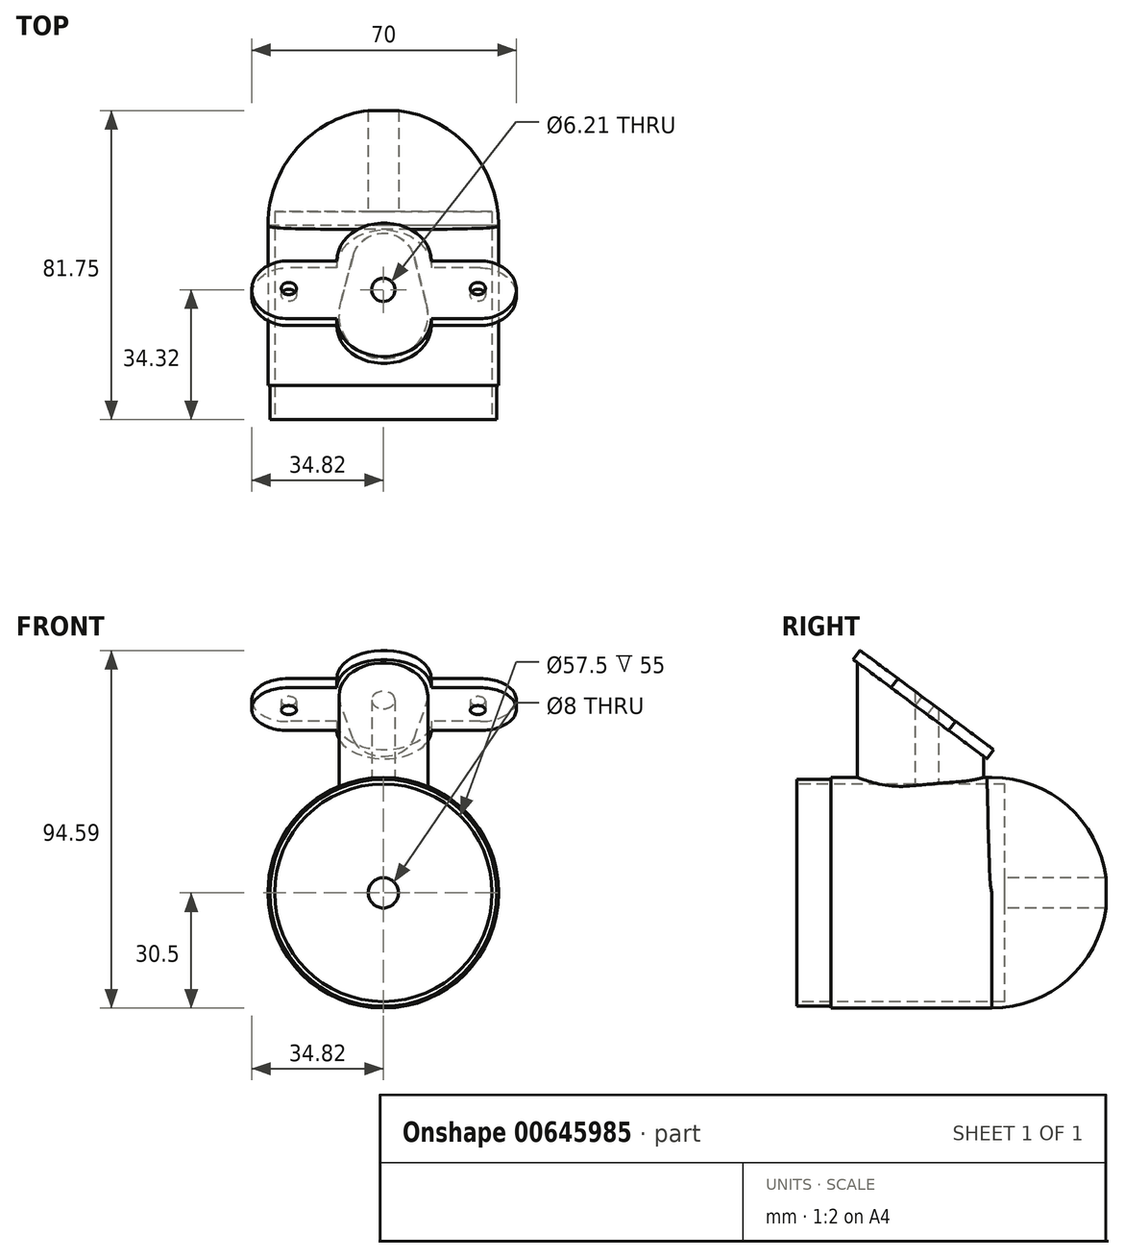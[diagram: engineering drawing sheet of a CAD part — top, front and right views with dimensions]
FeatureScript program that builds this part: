
annotation { "Feature Type Name" : "Feature", "Feature Type Description" : "" }
export const myFeature = defineFeature(function(context is Context, id is Id, definition is map)
    precondition{}
    {
        {
            var Q0;
            Q0=qCreatedBy(makeId("Front.planeOp"),FACE);
            var sketch = newSketch(context, id + "F0", { "sketchPlane" : qUnion([Q0])});
            skCircle(sketch, "E0", {"center": v(0, 0) * mm, "radius": 30.5 * mm});
            skSolve(sketch);
        }
        {
            var Q0;
            Q0 = qSketchRegion(id + "F0", true);
            extrude(context, id + "F1", {"entities" : qUnion([Q0]), "oppositeDirection" : true, "depth" : 54.5 * mm, "offsetDistance" : 25 * mm});
        }
        {
            var Q0;
            Q0=qCreatedBy(makeId("Right.planeOp"),FACE);
            var sketch = newSketch(context, id + "F2", { "sketchPlane" : qUnion([Q0])});
            skLineSegment(sketch, "E1", {"start": v(54.51, 30.53) * mm, "end": v(54.51, -30.47) * mm});
            skArc(sketch, "E2", {"start": v(54.51, -30.47) * mm, "mid": v(85.01, 0.03) * mm, "end": v(54.51, 30.53) * mm});
            skSolve(sketch);
        }
        {
            var Q0;
            Q0 = qSketchRegion(id + "F2", true);
            var Q1;
            Q1=sQuery(id+"F2.wireOp",EDGE,"E1");
            revolve(context, id + "F3", {"operationType" : NewBodyOperationType.ADD, "entities" : qUnion([Q0]), "axis" : qUnion([Q1]), "revolveType" : RevolveType.FULL});
        }
        {
            var Q0;
            Q0=qCreatedBy(makeId("Front.planeOp"),FACE);
            var sketch = newSketch(context, id + "F4", { "sketchPlane" : qUnion([Q0])});
            skCircle(sketch, "E3", {"center": v(0, 0) * mm, "radius": 44.94 * mm});
            skSolve(sketch);
        }
        {
            var Q0;
            Q0 = qSketchRegion(id + "F4", true);
            extrude(context, id + "F5", {"entities" : qUnion([Q0]), "operationType" : NewBodyOperationType.REMOVE, "oppositeDirection" : true, "depth" : 3 * mm, "offsetDistance" : 25 * mm});
        }
        {
            var Q0;
            Q0=qCreatedBy(makeId("Top.planeOp"),FACE);
            var sketch = newSketch(context, id + "F6", { "sketchPlane" : qUnion([Q0])});
            skLineSegment(sketch, "E4", {"start": v(-11.34, 33.76) * mm, "end": v(11.36, 33.76) * mm});
            skArc(sketch, "E5", {"start": v(-11.34, 33.76) * mm, "mid": v(0.01, 19) * mm, "end": v(11.36, 33.76) * mm});
            skLineSegment(sketch, "E6", {"start": v(-11.34, 33.76) * mm, "end": v(-8.04, 46.18) * mm});
            skLineSegment(sketch, "E7", {"start": v(11.36, 33.76) * mm, "end": v(8.06, 46.18) * mm});
            skLineSegment(sketch, "E8", {"start": v(-8.04, 46.18) * mm, "end": v(8.06, 46.18) * mm});
            skArc(sketch, "E9", {"start": v(8.06, 46.18) * mm, "mid": v(0.01, 52.37) * mm, "end": v(-8.04, 46.18) * mm});
            skSolve(sketch);
        }
        {
            var Q0;
            Q0 = qSketchRegion(id + "F6", true);
            extrude(context, id + "F7", {"entities" : qUnion([Q0]), "operationType" : NewBodyOperationType.ADD, "depth" : 70 * mm, "offsetDistance" : 25 * mm});
        }
        {
            var Q0;
            Q0=qCreatedBy(makeId("Front.planeOp"),FACE);
            var sketch = newSketch(context, id + "F8", { "sketchPlane" : qUnion([Q0])});
            skCircle(sketch, "E10", {"center": v(0, 0) * mm, "radius": 28.75 * mm});
            skSolve(sketch);
        }
        {
            var Q0;
            Q0 = qSketchRegion(id + "F8", true);
            extrude(context, id + "F9", {"entities" : qUnion([Q0]), "operationType" : NewBodyOperationType.REMOVE, "oppositeDirection" : true, "depth" : 58 * mm, "offsetDistance" : 25 * mm});
        }
        {
            var Q0;
            Q0=qCreatedBy(makeId("Right.planeOp"),FACE);
            var sketch = newSketch(context, id + "F10", { "sketchPlane" : qUnion([Q0])});
            skLineSegment(sketch, "E11", {"start": v(9.64, 68.83) * mm, "end": v(61.73, 29.95) * mm});
            skSolve(sketch);
        }
        {
            var Q0;
            Q0=qCreatedBy(makeId("Right.planeOp"),FACE);
            var sketch = newSketch(context, id + "F11", { "sketchPlane" : qUnion([Q0])});
            skLineSegment(sketch, "E12", {"start": v(7.22, 69.6) * mm, "end": v(59.4, 30.84) * mm});
            skSolve(sketch);
        }
        {
            var Q0;
            Q0=sQuery(id+"F11.wireOp",EDGE,"E12");
            extrude(context, id + "F12", {"bodyType" : ToolBodyType.SURFACE, "surfaceEntities" : qUnion([Q0]), "depth" : 25 * mm, "offsetDistance" : 25 * mm, "hasSecondDirection" : true, "secondDirectionOppositeDirection" : true, "secondDirectionDepth" : 25 * mm});
        }
        {
            var Q0;
            Q0=makeQuery(id+"F12.opExtrude","SWEPT_FACE",FACE,{"disambiguationData":[OSD([sQuery(id+"F11.wireOp",EDGE,"E12")])]});
            cPlane(context, id + "F13", {"entities" : qUnion([Q0]), "cplaneType" : CPlaneType.OFFSET, "offset" : 0 * mm, "width" : 150 * mm, "height" : 150 * mm});
        }
        {
            var Q0;
            Q0=makeQuery(id+"F12.opExtrude","SWEPT_FACE",FACE,{"disambiguationData":[OSD([sQuery(id+"F11.wireOp",EDGE,"E12")])]});
            extrude(context, id + "F14", {"entities" : qUnion([Q0]), "operationType" : NewBodyOperationType.REMOVE, "oppositeDirection" : true, "depth" : 30 * mm, "offsetDistance" : 25 * mm});
        }
        {
            var Q0;
            Q0=qCreatedBy(makeId("Front.planeOp"),FACE);
            var sketch = newSketch(context, id + "F15", { "sketchPlane" : qUnion([Q0])});
            skCircle(sketch, "E13", {"center": v(0, 0) * mm, "radius": 33.4 * mm});
            skCircle(sketch, "E14", {"center": v(0, 0) * mm, "radius": 30 * mm});
            skSolve(sketch);
        }
        {
            var Q0;
            Q0=makeQuery(id+"F15.imprint","IMPRINT",FACE,{"disambiguationData":[TD([[makeQuery(id+"F15.imprint","IMPRINT",EDGE,{"derivedFrom":sQuery(id+"F15.wireOp",EDGE,"E13")}),1.0]])]});
            var Q1;
            Q1=sQuery(id+"F15.wireOp",EDGE,"E14");
            var Q2;
            Q2=sQuery(id+"F15.wireOp",EDGE,"E13");
            extrude(context, id + "F16", {"entities" : qUnion([Q0]), "operationType" : NewBodyOperationType.REMOVE, "surfaceEntities" : qUnion([Q1, Q2]), "oppositeDirection" : true, "depth" : 12 * mm, "offsetDistance" : 25 * mm});
        }
        {
            var Q0;
            Q0=qCreatedBy(id+"F13.planeOp",FACE);
            var sketch = newSketch(context, id + "F17", { "sketchPlane" : qUnion([Q0])});
            skLineSegment(sketch, "E15", {"start": v(25.68, -9.08) * mm, "end": v(12.68, -9.08) * mm});
            skLineSegment(sketch, "E16", {"start": v(-12.32, -9.08) * mm, "end": v(-25.32, -9.08) * mm});
            skLineSegment(sketch, "E17", {"start": v(-25.32, 9.92) * mm, "end": v(-12.32, 9.92) * mm});
            skLineSegment(sketch, "E18", {"start": v(12.68, 9.92) * mm, "end": v(25.68, 9.92) * mm});
            skArc(sketch, "E19", {"start": v(25.68, -9.08) * mm, "mid": v(35.18, 0.42) * mm, "end": v(25.68, 9.92) * mm});
            skArc(sketch, "E20", {"start": v(-25.32, 9.92) * mm, "mid": v(-34.82, 0.42) * mm, "end": v(-25.32, -9.08) * mm});
            skArc(sketch, "E21", {"start": v(12.68, 9.92) * mm, "mid": v(0.18, 22.42) * mm, "end": v(-12.32, 9.92) * mm});
            skArc(sketch, "E22", {"start": v(-12.32, -9.08) * mm, "mid": v(0.18, -21.58) * mm, "end": v(12.68, -9.08) * mm});
            skSolve(sketch);
        }
        {
            var Q0;
            Q0=makeQuery(id+"F17.imprint","IMPRINT",FACE,{"disambiguationData":[TD([[makeQuery(id+"F17.imprint","IMPRINT",EDGE,{"derivedFrom":sQuery(id+"F17.wireOp",EDGE,"E15")}),-1.0]])]});
            extrude(context, id + "F18", {"entities" : qUnion([Q0]), "operationType" : NewBodyOperationType.ADD, "oppositeDirection" : true, "depth" : 3 * mm, "offsetDistance" : 25 * mm});
        }
        {
            var Q0;
            Q0=qCreatedBy(id+"F13.planeOp",FACE);
            var sketch = newSketch(context, id + "F19", { "sketchPlane" : qUnion([Q0])});
            skCircle(sketch, "E23", {"center": v(25, 0) * mm, "radius": 2 * mm});
            skCircle(sketch, "E24", {"center": v(-25, 0) * mm, "radius": 2 * mm});
            skSolve(sketch);
        }
        {
            var Q0;
            Q0 = qSketchRegion(id + "F19", true);
            extrude(context, id + "F20", {"entities" : qUnion([Q0]), "operationType" : NewBodyOperationType.REMOVE, "oppositeDirection" : true, "depth" : 25 * mm, "offsetDistance" : 25 * mm});
        }
        {
            var Q0;
            Q0=qCreatedBy(makeId("Top.planeOp"),FACE);
            var sketch = newSketch(context, id + "F21", { "sketchPlane" : qUnion([Q0])});
            skCircle(sketch, "E25", {"center": v(0, 37.32) * mm, "radius": 3.1 * mm});
            skSolve(sketch);
        }
        {
            var Q0;
            Q0 = qSketchRegion(id + "F21", true);
            extrude(context, id + "F22", {"entities" : qUnion([Q0]), "operationType" : NewBodyOperationType.REMOVE, "endBound" : BoundingType.THROUGH_ALL, "depth" : 25 * mm, "offsetDistance" : 25 * mm});
        }
        {
            var Q0;
            Q0=qCreatedBy(makeId("Front.planeOp"),FACE);
            var sketch = newSketch(context, id + "F23", { "sketchPlane" : qUnion([Q0])});
            skCircle(sketch, "E26", {"center": v(0, 0) * mm, "radius": 4 * mm});
            skSolve(sketch);
        }
        {
            var Q0;
            Q0 = qSketchRegion(id + "F23", true);
            extrude(context, id + "F24", {"entities" : qUnion([Q0]), "operationType" : NewBodyOperationType.REMOVE, "endBound" : BoundingType.THROUGH_ALL, "oppositeDirection" : true, "depth" : 25 * mm, "offsetDistance" : 25 * mm});
        }
    });
